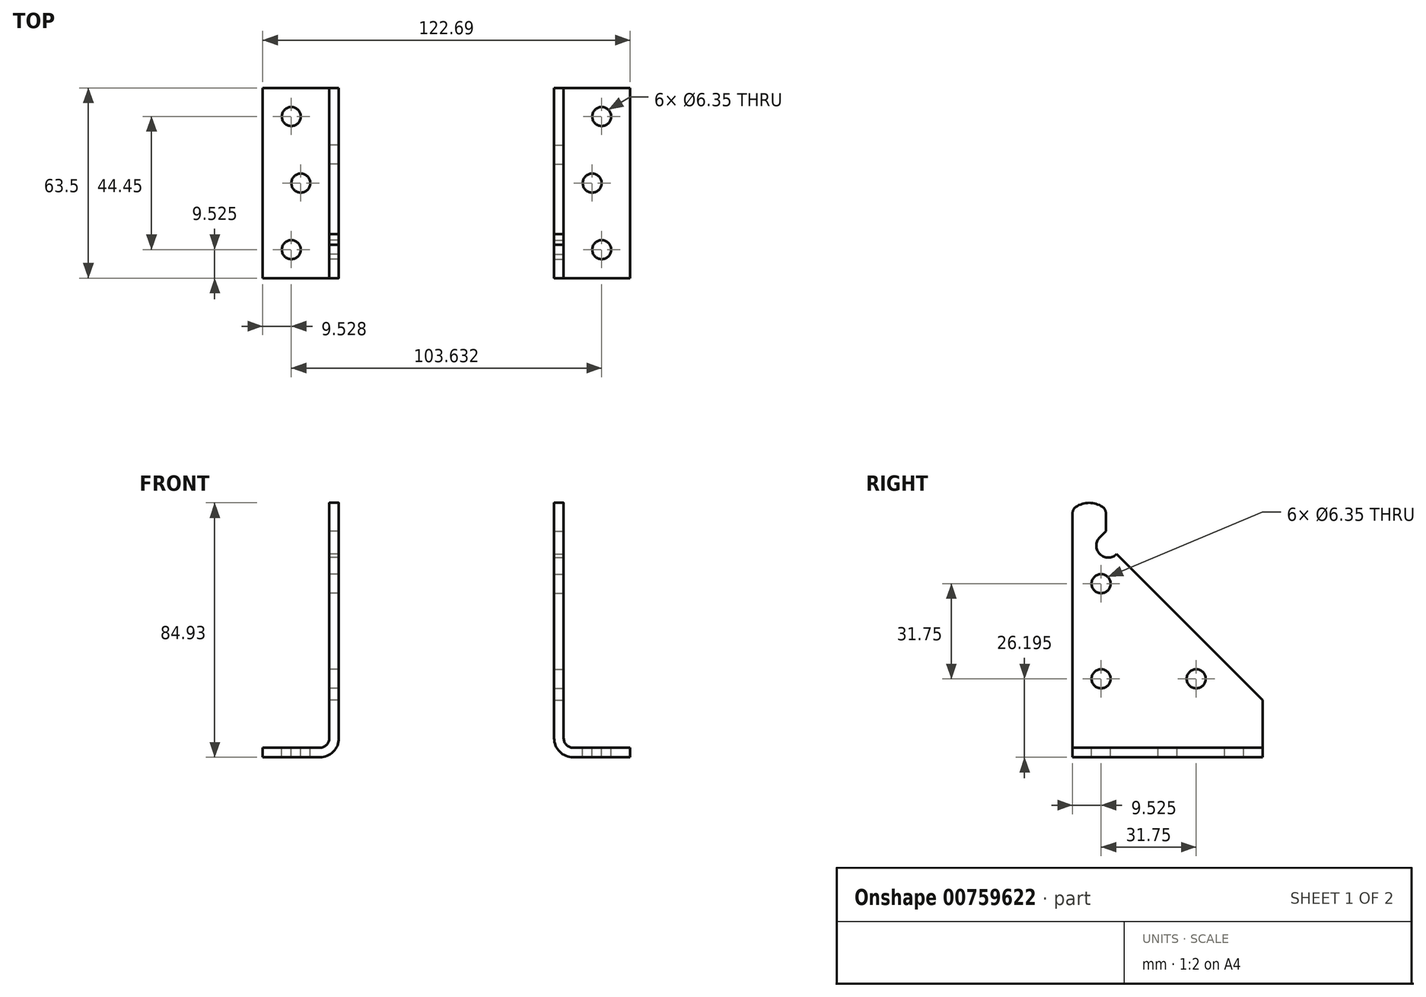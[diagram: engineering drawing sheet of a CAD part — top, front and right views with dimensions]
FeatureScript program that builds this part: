
annotation { "Feature Type Name" : "Feature", "Feature Type Description" : "" }
export const myFeature = defineFeature(function(context is Context, id is Id, definition is map)
    precondition{}
    {
        {
            var Q0;
            Q0=qCreatedBy(makeId("Right.planeOp"),FACE);
            var sketch = newSketch(context, id + "F0", { "sketchPlane" : qUnion([Q0])});
            skArc(sketch, "E0", {"start": v(-53.51, 77.23) * mm, "mid": v(-57.95, 78.58) * mm, "end": v(-62.38, 77.23) * mm});
            skLineSegment(sketch, "E1", {"start": v(-63.5, 75.12) * mm, "end": v(-63.5, 0) * mm});
            skLineSegment(sketch, "E2", {"start": v(-63.5, 0) * mm, "end": v(0, 0) * mm});
            skLineSegment(sketch, "E3", {"start": v(0, 0) * mm, "end": v(0, 12.7) * mm});
            skLineSegment(sketch, "E4", {"start": v(0, 12.7) * mm, "end": v(-48.79, 61.49) * mm});
            skLineSegment(sketch, "E5", {"start": v(-52.4, 75.12) * mm, "end": v(-52.4, 69.11) * mm});
            skLineSegment(sketch, "E6", {"start": v(-52.4, 69.11) * mm, "end": v(-54.4, 67.1) * mm});
            skArc(sketch, "E7", {"start": v(-54.4, 67.1) * mm, "mid": v(-54.4, 61.49) * mm, "end": v(-48.79, 61.49) * mm});
            skCircle(sketch, "E8", {"center": v(-53.97, 51.6) * mm, "radius": 3.18 * mm});
            skCircle(sketch, "E9", {"center": v(-53.97, 19.85) * mm, "radius": 3.18 * mm});
            skCircle(sketch, "E10", {"center": v(-22.22, 19.85) * mm, "radius": 3.18 * mm});
            skLineSegment(sketch, "E11", {"start": v(-51.6, 64.3) * mm, "end": v(-48.79, 61.49) * mm, "construction": true});
            skLineSegment(sketch, "E12", {"start": v(-51.6, 64.3) * mm, "end": v(-54.4, 67.1) * mm, "construction": true});
            skPoint(sketch, "E13.visualSharp", {"position": v(-63.5, 76.31) * mm});
            skArc(sketch, "E13.filletArc", {"start": v(-62.38, 77.23) * mm, "mid": v(-63.2, 76.32) * mm, "end": v(-63.5, 75.12) * mm});
            skPoint(sketch, "E14.visualSharp", {"position": v(-52.4, 76.31) * mm});
            skArc(sketch, "E14.filletArc", {"start": v(-52.4, 75.12) * mm, "mid": v(-52.69, 76.32) * mm, "end": v(-53.51, 77.23) * mm});
            skSolve(sketch);
        }
        {
            var Q0;
            Q0=makeQuery(id+"F0.imprint","IMPRINT",FACE,{"disambiguationData":[TD([[makeQuery(id+"F0.imprint","IMPRINT",EDGE,{"derivedFrom":sQuery(id+"F0.wireOp",EDGE,"E0")}),1.0]])]});
            extrude(context, id + "F1", {"entities" : qUnion([Q0]), "oppositeDirection" : true, "depth" : 3.17 * mm, "offsetDistance" : 25.4 * mm});
        }
        {
            var Q0;
            Q0=makeQuery(id+"F1.opExtrude","SWEPT_FACE",FACE,{"disambiguationData":[OSD([sQuery(id+"F0.wireOp",EDGE,"E1")])]});
            var sketch = newSketch(context, id + "F2", { "sketchPlane" : qUnion([Q0])});
            skArc(sketch, "E15", {"start": v(-3.18, 0) * mm, "mid": v(-1.32, -4.5) * mm, "end": v(3.17, -6.35) * mm});
            skLineSegment(sketch, "E16", {"start": v(3.18, -6.35) * mm, "end": v(22.23, -6.35) * mm});
            skLineSegment(sketch, "E17.0", {"start": v(-3.18, 0) * mm, "end": v(0, 0) * mm});
            skLineSegment(sketch, "E18.0", {"start": v(0, 75.12) * mm, "end": v(0, 0) * mm});
            skArc(sketch, "E19", {"start": v(0, 0) * mm, "mid": v(0.93, -2.25) * mm, "end": v(3.18, -3.17) * mm});
            skLineSegment(sketch, "E20", {"start": v(3.18, -3.17) * mm, "end": v(22.23, -3.17) * mm});
            skLineSegment(sketch, "E21", {"start": v(22.23, -3.17) * mm, "end": v(22.23, -6.35) * mm});
            skSolve(sketch);
        }
        {
            var Q0;
            Q0=makeQuery(id+"F2.imprint","IMPRINT",FACE,{"disambiguationData":[TD([[makeQuery(id+"F2.imprint","IMPRINT",EDGE,{"derivedFrom":sQuery(id+"F2.wireOp",EDGE,"E15")}),1.0]])]});
            var Q1;
            Q1=makeQuery(id+"F1.opExtrude","SWEPT_FACE",FACE,{"disambiguationData":[OSD([sQuery(id+"F0.wireOp",EDGE,"E3")])]});
            extrude(context, id + "F3", {"entities" : qUnion([Q0]), "operationType" : NewBodyOperationType.ADD, "endBound" : BoundingType.UP_TO_SURFACE, "oppositeDirection" : true, "depth" : 25.4 * mm, "endBoundEntityFace" : qUnion([Q1]), "offsetDistance" : 25.4 * mm});
        }
        {
            var Q0;
            Q0=makeQuery(id+"F3.opExtrude","SWEPT_FACE",FACE,{"disambiguationData":[OSD([sQuery(id+"F2.wireOp",EDGE,"E20")])]});
            var sketch = newSketch(context, id + "F4", { "sketchPlane" : qUnion([Q0])});
            skCircle(sketch, "E22", {"center": v(12.7, -53.97) * mm, "radius": 3.18 * mm});
            skCircle(sketch, "E23", {"center": v(9.52, -31.75) * mm, "radius": 3.18 * mm});
            skCircle(sketch, "E24", {"center": v(12.7, -9.53) * mm, "radius": 3.18 * mm});
            skSolve(sketch);
        }
        {
            var Q0;
            Q0=makeQuery(id+"F4.imprint","IMPRINT",FACE,{"disambiguationData":[TD([[makeQuery(id+"F4.imprint","IMPRINT",EDGE,{"derivedFrom":sQuery(id+"F4.wireOp",EDGE,"E22")}),1.0]])]});
            var Q1;
            Q1=makeQuery(id+"F4.imprint","IMPRINT",FACE,{"disambiguationData":[TD([[makeQuery(id+"F4.imprint","IMPRINT",EDGE,{"derivedFrom":sQuery(id+"F4.wireOp",EDGE,"E23")}),1.0]])]});
            var Q2;
            Q2=makeQuery(id+"F4.imprint","IMPRINT",FACE,{"disambiguationData":[TD([[makeQuery(id+"F4.imprint","IMPRINT",EDGE,{"derivedFrom":sQuery(id+"F4.wireOp",EDGE,"E24")}),1.0]])]});
            extrude(context, id + "F5", {"entities" : qUnion([Q0, Q1, Q2]), "operationType" : NewBodyOperationType.REMOVE, "endBound" : BoundingType.THROUGH_ALL, "oppositeDirection" : true, "depth" : 25.4 * mm, "offsetDistance" : 25.4 * mm});
        }
        {
            var Q0;
            Q0=qCreatedBy(makeId("Right.planeOp"),FACE);
            cPlane(context, id + "F6", {"entities" : qUnion([Q0]), "cplaneType" : CPlaneType.OFFSET, "offset" : 39.12 * mm, "oppositeDirection" : true, "width" : 152.4 * mm, "height" : 152.4 * mm});
        }
        {
            var Q0;
            Q0=makeQuery(id+"F1.opExtrude","SWEPT_BODY",BODY,{"disambiguationData":[OSD([sQuery(id+"F0.wireOp",EDGE,"E0"),sQuery(id+"F0.wireOp",EDGE,"E1"),sQuery(id+"F0.wireOp",EDGE,"E2"),sQuery(id+"F0.wireOp",EDGE,"E3"),sQuery(id+"F0.wireOp",EDGE,"E4"),sQuery(id+"F0.wireOp",EDGE,"E5"),sQuery(id+"F0.wireOp",EDGE,"E6"),sQuery(id+"F0.wireOp",EDGE,"E7"),sQuery(id+"F0.wireOp",EDGE,"E8"),sQuery(id+"F0.wireOp",EDGE,"E9"),sQuery(id+"F0.wireOp",EDGE,"E10"),sQuery(id+"F0.wireOp",EDGE,"E13.filletArc"),sQuery(id+"F0.wireOp",EDGE,"E14.filletArc")])]});
            var Q1;
            Q1=qCreatedBy(id+"F6.planeOp",FACE);
            mirror(context, id + "F7", {"entities" : qUnion([Q0]), "mirrorPlane" : qUnion([Q1])});
        }
    });
